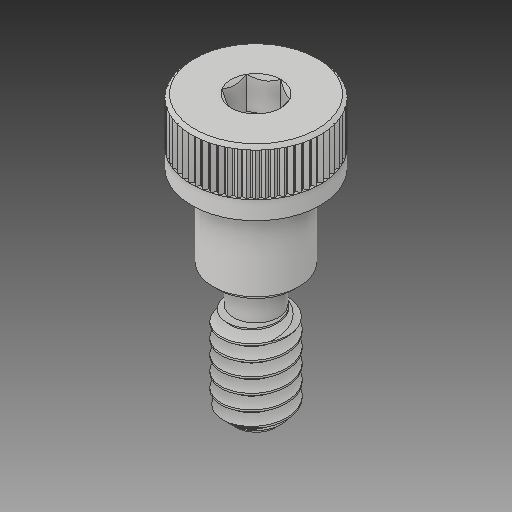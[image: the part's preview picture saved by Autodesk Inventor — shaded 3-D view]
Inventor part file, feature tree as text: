
AUTODESK INVENTOR PART (.ipt)
format: ipt  version: 2017 (Build 210142000, 142)  size: 586,752 bytes
history: native  units: in
note: dims shown in document units (in); Inventor stores cm internally (conversion verified against a paired STEP export)
features: chamfer x1
ambient origin geometry x8: Origin, YZ Plane, XZ Plane, XY Plane, X Axis, Y Axis, Z Axis, Center Point
bodies: Solid1 (feature_tree)
feature tree (1):
  chamfer  "Chamfer3"  [1 undecoded]
note: 1 required parameter value undecoded (feature->parameter linkage not recoverable at this tier; creation-order binding heuristic only, values carry confidence <= 0.55)
